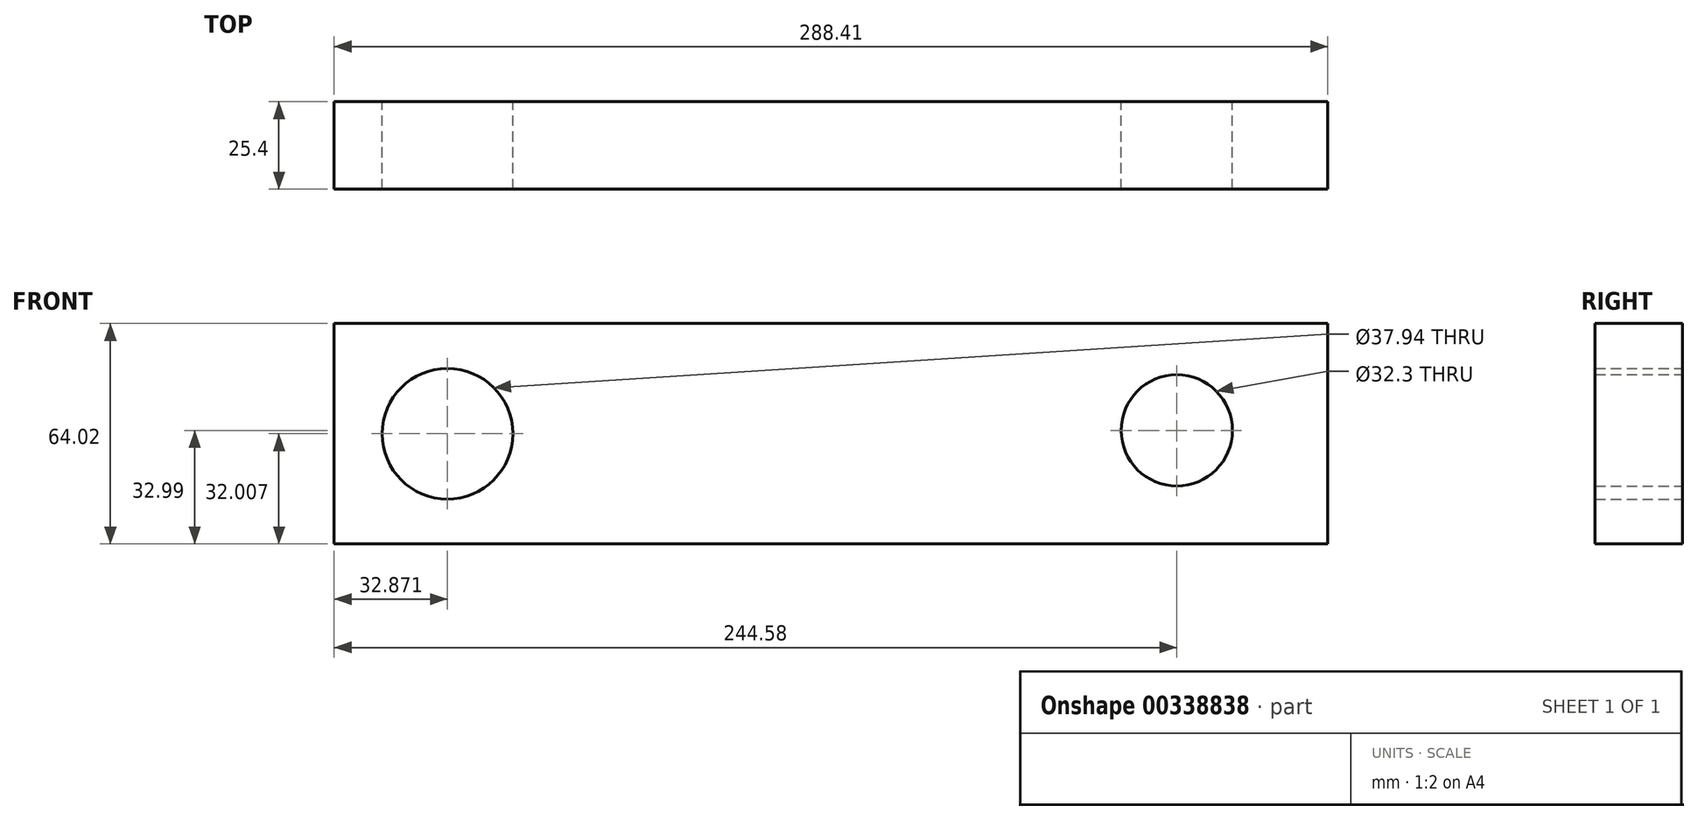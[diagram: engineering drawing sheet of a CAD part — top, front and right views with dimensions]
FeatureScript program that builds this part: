
annotation { "Feature Type Name" : "Feature", "Feature Type Description" : "" }
export const myFeature = defineFeature(function(context is Context, id is Id, definition is map)
    precondition{}
    {
        {
            var Q0;
            Q0=qCreatedBy(makeId("Front.planeOp"),FACE);
            var sketch = newSketch(context, id + "F0", { "sketchPlane" : qUnion([Q0])});
            skLineSegment(sketch, "E0.bottom", {"start": v(-127.11, 31.03) * mm, "end": v(161.3, 31.03) * mm});
            skLineSegment(sketch, "E0.top", {"start": v(-127.11, -33) * mm, "end": v(161.3, -33) * mm});
            skLineSegment(sketch, "E0.left", {"start": v(-127.11, 31.03) * mm, "end": v(-127.11, -33) * mm});
            skLineSegment(sketch, "E0.right", {"start": v(161.3, 31.03) * mm, "end": v(161.3, -33) * mm});
            skCircle(sketch, "E1", {"center": v(-94.24, -0.98) * mm, "radius": 18.97 * mm});
            skPoint(sketch, "E1.centerSnap0", {"position": v(-127.11, -0.98) * mm});
            skCircle(sketch, "E2", {"center": v(117.47, 0) * mm, "radius": 16.15 * mm});
            skSolve(sketch);
        }
        {
            var Q0;
            Q0 = qSketchRegion(id + "F0", true);
            extrude(context, id + "F1", {"entities" : qUnion([Q0]), "depth" : 25.4 * mm});
        }
    });
